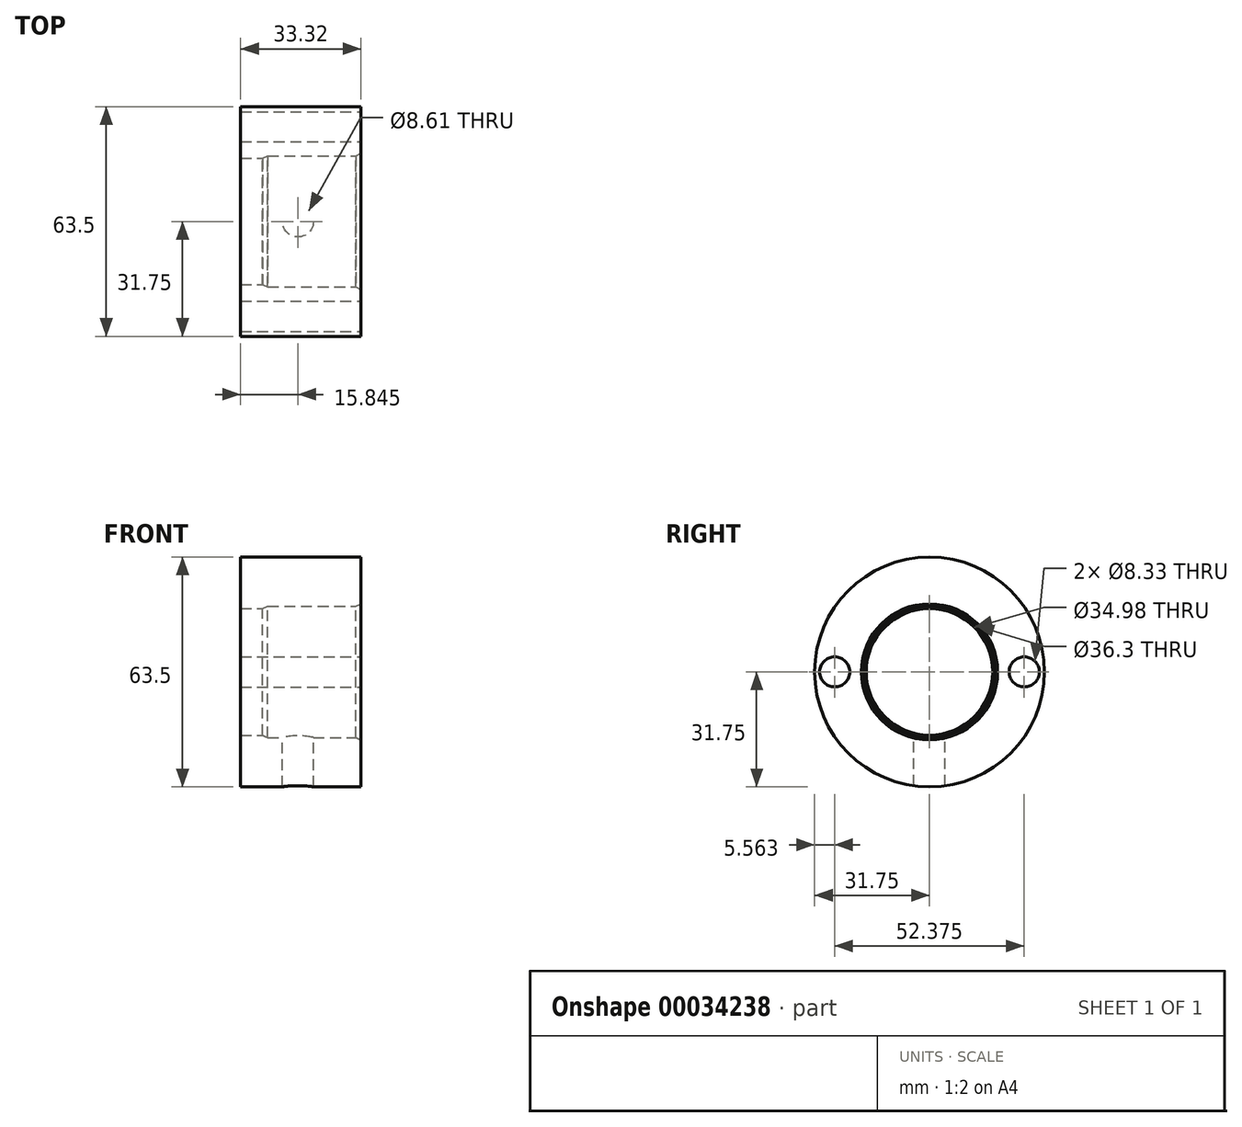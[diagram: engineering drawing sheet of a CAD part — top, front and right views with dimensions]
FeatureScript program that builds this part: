
annotation { "Feature Type Name" : "Feature", "Feature Type Description" : "" }
export const myFeature = defineFeature(function(context is Context, id is Id, definition is map)
    precondition{}
    {
        {
            var Q0;
            Q0=qCreatedBy(makeId("Right.planeOp"),FACE);
            var sketch = newSketch(context, id + "F0", { "sketchPlane" : qUnion([Q0])});
            skCircle(sketch, "E0", {"center": v(0, 0) * mm, "radius": 31.75 * mm});
            skCircle(sketch, "E1", {"center": v(26.19, 0) * mm, "radius": 4.17 * mm});
            skCircle(sketch, "E2.1.0", {"center": v(-26.19, 0) * mm, "radius": 4.17 * mm});
            skSolve(sketch);
        }
        {
            var Q0;
            Q0=makeQuery(id+"F0.imprint","IMPRINT",FACE,{"disambiguationData":[TD([[makeQuery(id+"F0.imprint","IMPRINT",EDGE,{"derivedFrom":sQuery(id+"F0.wireOp",EDGE,"E0")}),1.0]])]});
            extrude(context, id + "F1", {"entities" : qUnion([Q0]), "oppositeDirection" : true, "depth" : 33.32 * mm});
        }
        {
            var Q0;
            Q0=qCreatedBy(makeId("Front.planeOp"),FACE);
            var sketch = newSketch(context, id + "F2", { "sketchPlane" : qUnion([Q0])});
            skLineSegment(sketch, "E3", {"start": v(-1.42, 18.15) * mm, "end": v(-25.8, 18.15) * mm});
            skLineSegment(sketch, "E4", {"start": v(-27.22, 17.49) * mm, "end": v(-34.93, 17.49) * mm});
            skLineSegment(sketch, "E5", {"start": v(-34.93, 17.49) * mm, "end": v(-34.93, 0) * mm});
            skLineSegment(sketch, "E6", {"start": v(-34.93, 0) * mm, "end": v(0, 0) * mm});
            skPoint(sketch, "E7.orphan", {"position": v(1.57, 18.15) * mm});
            skPoint(sketch, "E8.orphan", {"position": v(1.57, 0) * mm});
            skLineSegment(sketch, "E9", {"start": v(-25.8, 18.15) * mm, "end": v(-27.22, 17.49) * mm});
            skLineSegment(sketch, "E10", {"start": v(-1.42, 18.15) * mm, "end": v(0, 18.81) * mm});
            skLineSegment(sketch, "E11", {"start": v(0, 0) * mm, "end": v(0, 18.81) * mm});
            skPoint(sketch, "E12.orphan", {"position": v(0, 18.15) * mm});
            skSolve(sketch);
        }
        {
            var Q0;
            Q0 = qSketchRegion(id + "F2", true);
            var Q1;
            Q1=sQuery(id+"F2.wireOp",EDGE,"E6");
            revolve(context, id + "F3", {"operationType" : NewBodyOperationType.REMOVE, "entities" : qUnion([Q0]), "axis" : qUnion([Q1]), "revolveType" : RevolveType.FULL, "oppositeDirection" : true});
        }
        {
            var Q0;
            Q0=qCreatedBy(makeId("Top.planeOp"),FACE);
            var sketch = newSketch(context, id + "F4", { "sketchPlane" : qUnion([Q0])});
            skCircle(sketch, "E13", {"center": v(-17.48, 0) * mm, "radius": 4.3 * mm});
            skSolve(sketch);
        }
        {
            var Q0;
            Q0=makeQuery(id+"F4.imprint","IMPRINT",FACE,{"disambiguationData":[TD([[makeQuery(id+"F4.imprint","IMPRINT",EDGE,{"derivedFrom":sQuery(id+"F4.wireOp",EDGE,"E13")}),1.0]])]});
            extrude(context, id + "F5", {"entities" : qUnion([Q0]), "operationType" : NewBodyOperationType.REMOVE, "oppositeDirection" : true, "depth" : 32.5 * mm});
        }
    });
